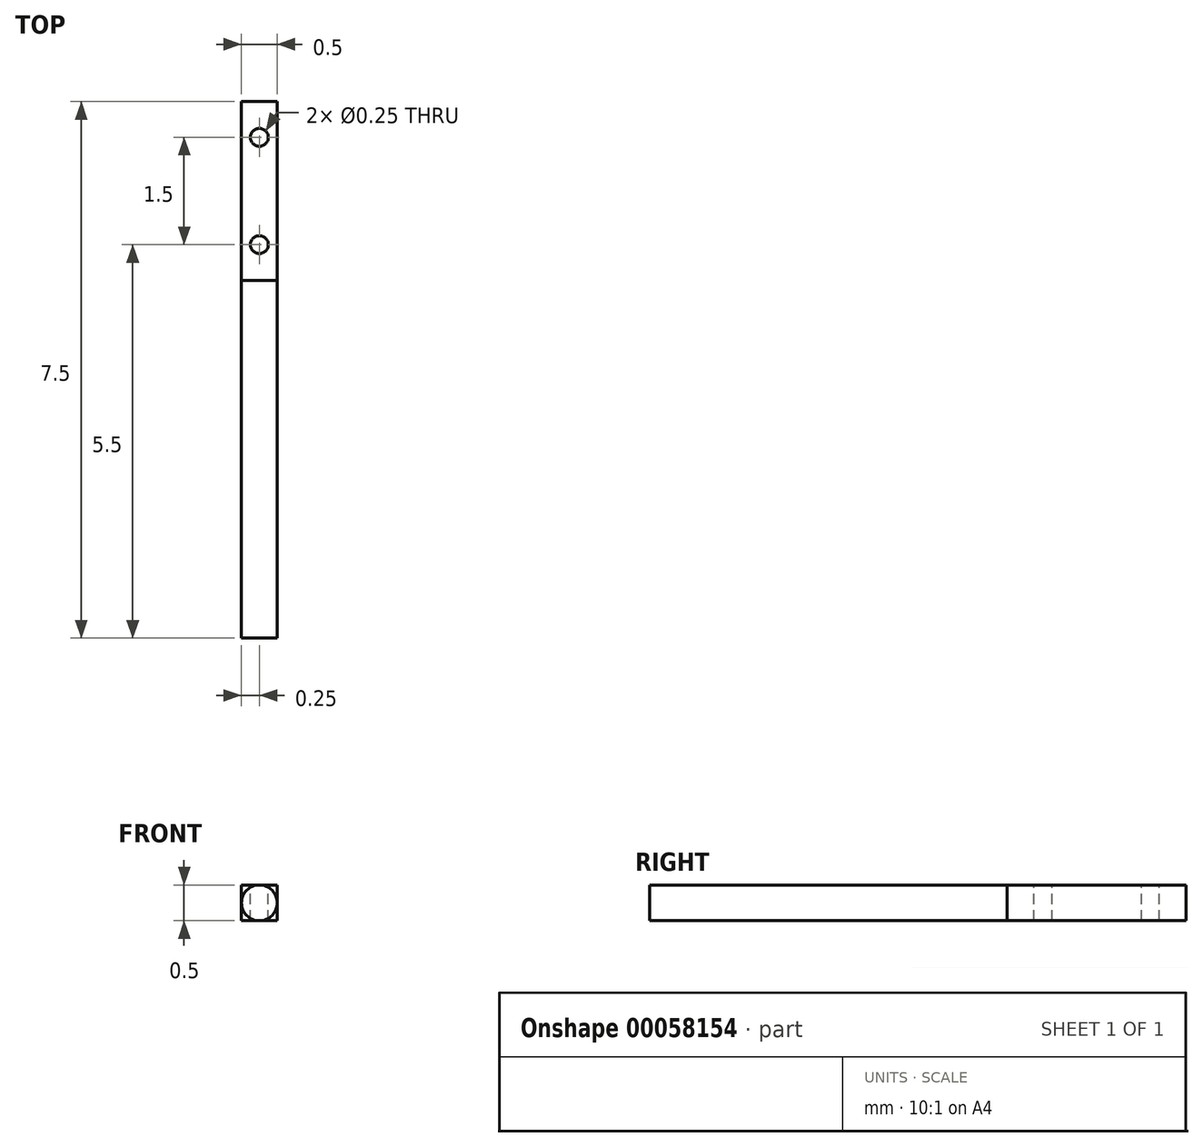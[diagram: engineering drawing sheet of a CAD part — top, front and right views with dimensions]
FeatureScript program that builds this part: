
annotation { "Feature Type Name" : "Feature", "Feature Type Description" : "" }
export const myFeature = defineFeature(function(context is Context, id is Id, definition is map)
    precondition{}
    {
        {
            var Q0;
            Q0=qCreatedBy(makeId("Front.planeOp"),FACE);
            var sketch = newSketch(context, id + "F0", { "sketchPlane" : qUnion([Q0])});
            skCircle(sketch, "E0", {"center": v(0, 0) * mm, "radius": 0.25 * mm});
            skSolve(sketch);
        }
        {
            var Q0;
            Q0 = qSketchRegion(id + "F0", true);
            extrude(context, id + "F1", {"entities" : qUnion([Q0]), "endBound" : BoundingType.SYMMETRIC, "depth" : 7.5 * mm});
        }
        {
            var Q0;
            Q0=makeQuery(id+"F1.opExtrude","CAP_FACE",FACE,{"disambiguationData":[OSD([sQuery(id+"F0.wireOp",EDGE,"E0")])],"isStart":true});
            var sketch = newSketch(context, id + "F2", { "sketchPlane" : qUnion([Q0])});
            skLineSegment(sketch, "E1.rect.bottom", {"start": v(0.25, 0.25) * mm, "end": v(-0.25, 0.25) * mm});
            skLineSegment(sketch, "E1.rect.top", {"start": v(0.25, -0.25) * mm, "end": v(-0.25, -0.25) * mm});
            skLineSegment(sketch, "E1.rect.left", {"start": v(0.25, 0.25) * mm, "end": v(0.25, -0.25) * mm});
            skLineSegment(sketch, "E1.rect.right", {"start": v(-0.25, 0.25) * mm, "end": v(-0.25, -0.25) * mm});
            skPoint(sketch, "E1.rect.middle", {"position": v(0, 0) * mm});
            skSolve(sketch);
        }
        {
            var Q0;
            Q0 = qSketchRegion(id + "F2", true);
            extrude(context, id + "F3", {"entities" : qUnion([Q0]), "operationType" : NewBodyOperationType.ADD, "oppositeDirection" : true, "depth" : 2.5 * mm});
        }
        {
            var Q0;
            Q0=makeQuery(id+"F3.opExtrude","SWEPT_FACE",FACE,{"disambiguationData":[OSD([sQuery(id+"F2.wireOp",EDGE,"E1.rect.bottom")])]});
            var sketch = newSketch(context, id + "F4", { "sketchPlane" : qUnion([Q0])});
            skCircle(sketch, "E2", {"center": v(0, 3.25) * mm, "radius": 0.12 * mm});
            skPoint(sketch, "E2.centerSnap0", {"position": v(0, 3.75) * mm});
            skCircle(sketch, "E3", {"center": v(0, 1.75) * mm, "radius": 0.12 * mm});
            skSolve(sketch);
        }
        {
            var Q0;
            Q0 = qSketchRegion(id + "F4", true);
            extrude(context, id + "F5", {"entities" : qUnion([Q0]), "operationType" : NewBodyOperationType.REMOVE, "oppositeDirection" : true, "depth" : 25 * mm});
        }
    });
